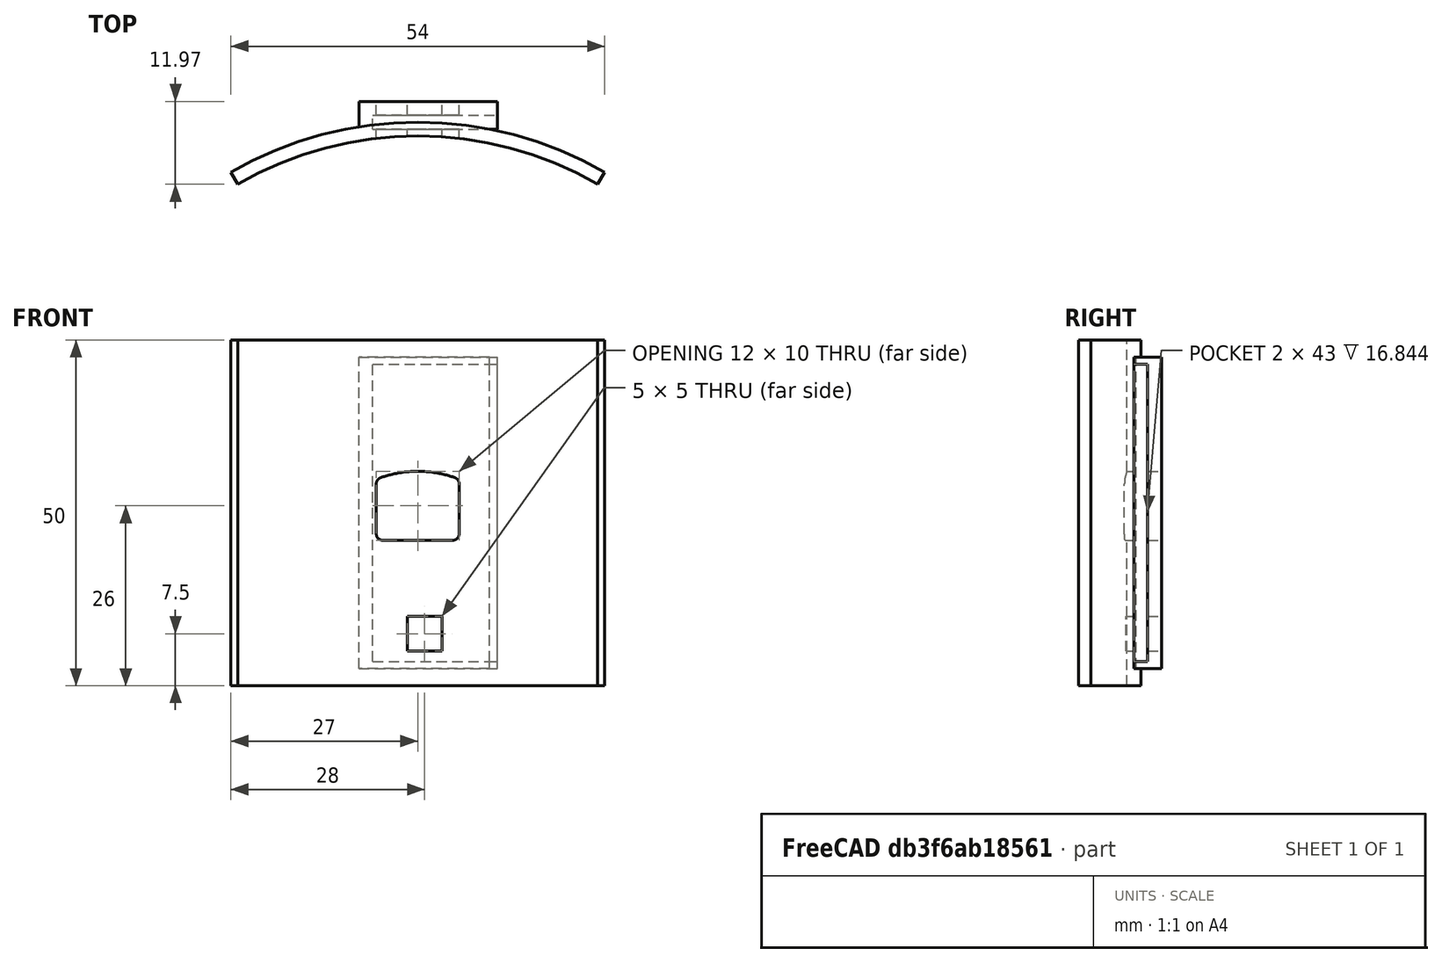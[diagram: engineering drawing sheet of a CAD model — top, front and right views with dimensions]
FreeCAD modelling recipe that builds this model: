
FCSTD DOCUMENT  (FreeCAD 0.16R4924 (Git))
Label: outer_latch_v2
License: All rights reserved
LicenseURL: http://en.wikipedia.org/wiki/All_rights_reserved
objects: Part::Cut×4, Part::Box×3, Part::MultiFuse×3, Part::Cylinder×2, Part::Feature×2, Part::Extrusion×2, Part::Thickness×1
note: 17 computed .brp shape members not serialized (recipe doc carries the construction recipe); baked Part::Feature solids carry a one-line shape summary decoded from their .brp

FEATURE [Part::Cylinder] Cylinder  label="bottle_wall"
  Angle = 60
  Height = 50
  Placement = pos=(8.5,-7,0) rot=(0,0,1;1.0472rad)
  Radius = 54
FEATURE [Part::Cylinder] Cylinder001  label="bottle_wall001"
  Angle = 60
  Height = 50
  Placement = pos=(8.5,-7,0) rot=(0,0,1;1.0472rad)
  Radius = 52
FEATURE [Part::Cut] Cut
  Base = -> Cylinder
  Placement = pos=(0,-2,0) rot=(0,0,1;0rad)
  Tool = -> Cylinder001
FEATURE [Part::Box] Box  label="pin_opening"
  Height = 5
  Length = 5
  Placement = pos=(7,42,5) rot=(0,0,1;0rad)
  Width = 20
FEATURE [Part::Box] Box001  label="latch"
  Height = 45
  Length = 20
  Placement = pos=(0,44,2.5) rot=(0,0,1;0rad)
  Width = 4
FEATURE [Part::MultiFuse] Fusion
  Shapes = -> [Cut,Box001]
FEATURE [Part::MultiFuse] Fusion001
  Shapes = -> [Fusion,Box001]
FEATURE [Part::Cut] Cut001
  Base = -> Fusion001
  Tool = -> Box
FEATURE [Part::Box] Box002  label="slot"
  Height = 43
  Length = 20
  Placement = pos=(2,44,3.5) rot=(0,0,1;0rad)
  Width = 2
FEATURE [Part::Cut] Cut002
  Base = -> Cut001
  Tool = -> Box002
FEATURE [Part::Feature] Common_cs001  label="pin_cs001"
  Placement = pos=(3.5,35,2) rot=(0,0,1;0rad)
  shape: bbox 10 x 2e-07 x 8 mm, 0 faces, 0 solids (baked)
FEATURE [Part::Extrusion] Extrude
  Base = -> Common_cs001
  Dir = (0,6,0)
  Solid = true
FEATURE [Part::Thickness] Thickness
  Faces = -> Extrude [Face7]
  Intersection = false
  Join = 0
  Mode = 0
  SelfIntersection = false
  Value = 1
FEATURE [Part::Feature] Common_cs002  label="pin_cs002"
  Placement = pos=(3.5,35,2) rot=(0,0,1;0rad)
  shape: bbox 10 x 2e-07 x 8 mm, 0 faces, 0 solids (baked)
FEATURE [Part::Extrusion] Extrude001
  Base = -> Common_cs002
  Dir = (0,6,0)
  Solid = true
FEATURE [Part::MultiFuse] Fusion002
  Placement = pos=(0,-3,20) rot=(0,0,1;0rad)
  Shapes = -> [Thickness,Extrude,Extrude001]
FEATURE [Part::Cut] Cut003
  Base = -> Cut002
  Tool = -> Fusion002
